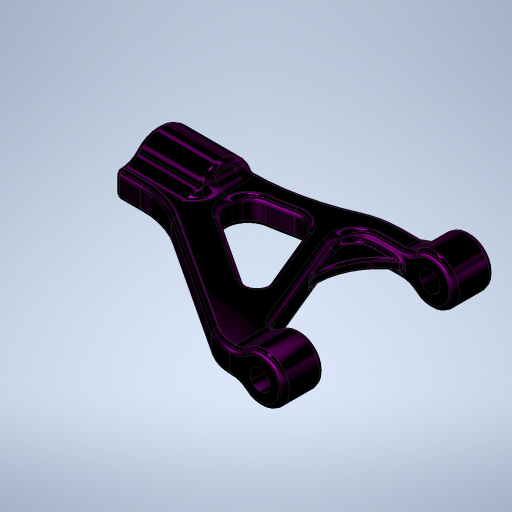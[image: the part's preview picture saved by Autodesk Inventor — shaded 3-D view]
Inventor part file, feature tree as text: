
AUTODESK INVENTOR PART (.ipt)
format: ipt  version: 2023.1 (Build 271208000, 208)  size: 986,112 bytes
history: native  units: in
note: dims shown in document units (in); Inventor stores cm internally (conversion verified against a paired STEP export)
features: fillet x15, sketch x10, extrude x6, hole x2, rib x2, projected_geometry x2, plane x1
ambient origin geometry x8: Origin, YZ Plane, XZ Plane, XY Plane, X Axis, Y Axis, Z Axis, Center Point
bodies: Solid1 (feature_tree)
feature tree (38):
  extrude  "Extrusion1"  Depth=0.25in TaperAngle=0.0deg
  plane  "Work Plane1"
  extrude  "Extrusion2"  Depth=0.25in TaperAngle=0.0deg
  extrude  "Extrusion3"  Depth=0.425in
  extrude  "Extrusion4"  Depth=1.5in
  fillet  "Fillet1"  Radius=0.163in
  fillet  "Fillet2"  Radius=0.125in
  extrude  "Extrusion5"  Depth=0.125in
  extrude  "Extrusion6"  Depth=0.135in
  fillet  "Fillet3"  Radius=0.5in
  fillet  "Fillet4"  Radius=0.365in
  fillet  "Fillet5"  Radius=0.5in
  fillet  "Fillet6"  Radius=0.1625in
  fillet  "Fillet7"  Radius=0.154in
  fillet  "Fillet8"  Radius=0.125in
  fillet  "Fillet9"  Radius=0.1625in
  fillet  "Fillet10"  Radius=0.125in
  fillet  "Fillet11"  Radius=0.0625in
  hole  "Hole1"  [1 undecoded]
  hole  "Hole2"  [1 undecoded]
  rib  "Rib2"
  fillet  "Fillet12"  Radius=0.415in
  fillet  "Fillet13"  Radius=0.125in
  rib  "Rib3"
  fillet  "Fillet14"  Radius=0.032in
  fillet  "Fillet15"  Radius=0.032in
  sketch  "Sketch1"  dims[d0=0.3in d1=0.25in d2=0.0in]
  sketch  "Sketch2"  dims[d3=0.8in d4=0.25in d5=0.0in]
  sketch  "Sketch3"  dims[d6=0.867in d7=0.425in]
  sketch  "Sketch4"  dims[d8=0.158in d9=1.5in d10=0.163in d11=0.125in]
  sketch  "Sketch5"  dims[d12=0.189in d13=0.125in]
  sketch  "Sketch6"  dims[d14=0.315in d15=0.135in d16=0.5in d17=0.365in d18=0.5in d19=0.1625in d20=0.0in d21=0.154in d22=0.125in d23=0.1625in d24=0.0in d25=0.125in d26=0.0625in]
  sketch  "Sketch8"  dims[d27=0.063in d28=0.1625in d29=0.0in]
  sketch  "Sketch9"  dims[d30=0.375in d32=0.1575in d33=0.415in d34=0.0in d35=0.125in d36=0.032in d37=0.032in]
  sketch  "Sketch11"  dims[d38=0.032in]
  sketch  "Sketch12"  dims[d39=0.0625in d40=0.032in d41=0.032in d42=0.0625in d43=0.032in d44=0.134in d45=0.328in d46=0.375in d47=0.25in d48=0.5635in d49=0.375in d50=0.8108in d51=0.125in d52=0.328in d53=0.375in d54=0.25in d55=0.5635in d56=0.375in d57=0.8108in d64=0.1in d65=0.0625in d66=0.0in d67=0.0in d68=0.1in d69=0.1in d70=0.015in d71=0.031in d72=0.1in d73=0.0625in d74=0.0in d75=0.0in d76=0.1in d77=0.1in d78=0.015in d79=0.031in]
  projected_geometry  "Project Cut Edges1"
  projected_geometry  "Project Cut Edges2"
note: 2 required parameter values undecoded (feature->parameter linkage not recoverable at this tier; creation-order binding heuristic only, values carry confidence <= 0.55)
